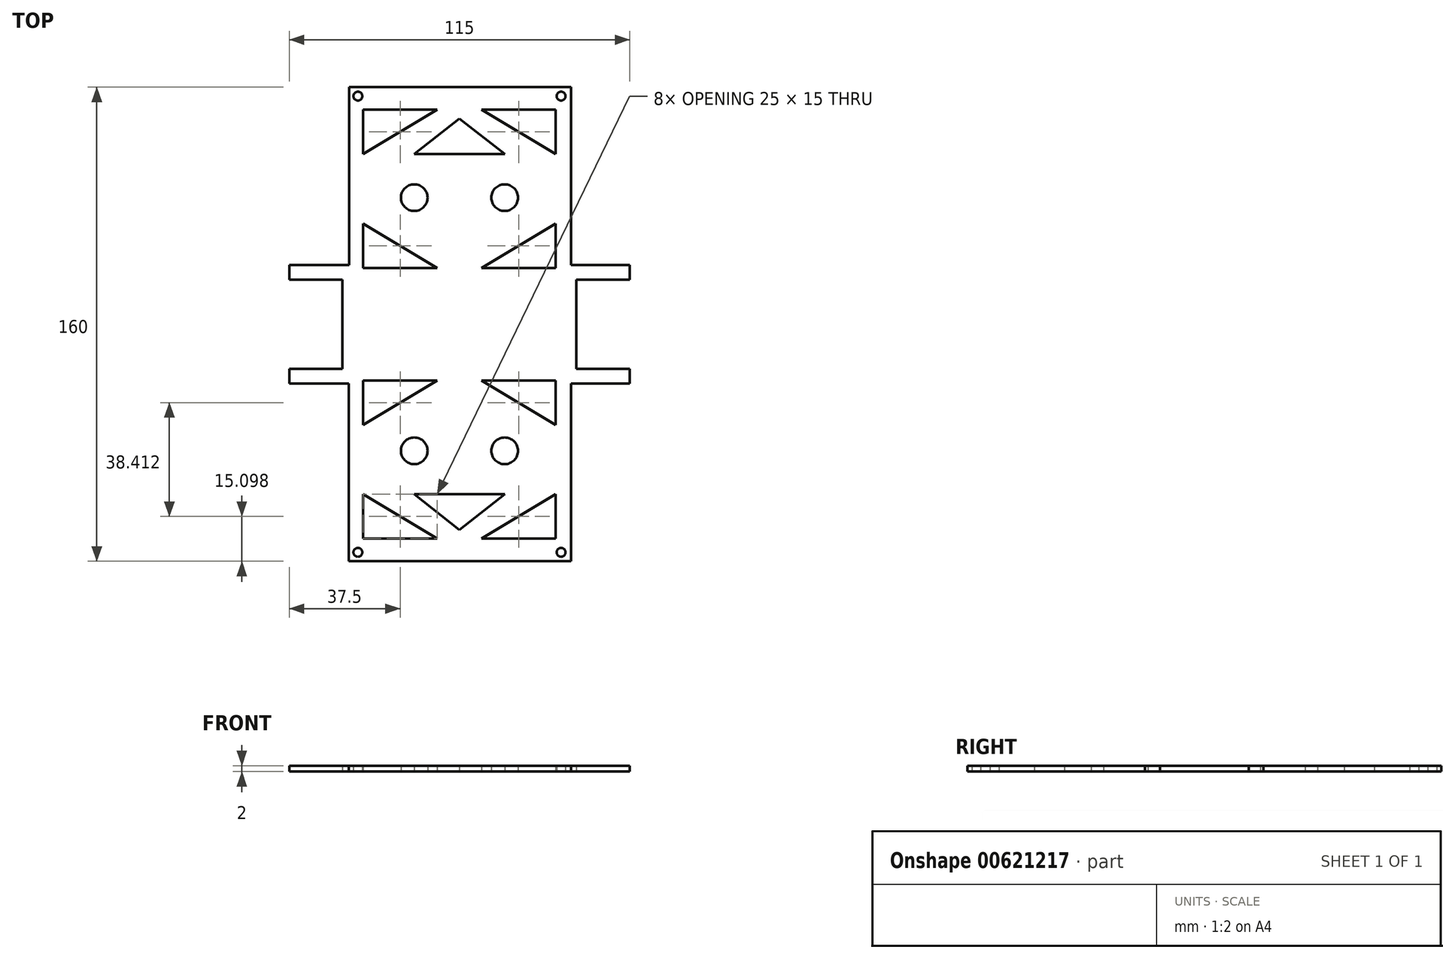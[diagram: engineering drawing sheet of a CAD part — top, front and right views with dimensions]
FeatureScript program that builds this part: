
annotation { "Feature Type Name" : "Feature", "Feature Type Description" : "" }
export const myFeature = defineFeature(function(context is Context, id is Id, definition is map)
    precondition{}
    {
        {
            var Q0;
            Q0=qCreatedBy(makeId("Top.planeOp"),FACE);
            var sketch = newSketch(context, id + "F0", { "sketchPlane" : qUnion([Q0])});
            skLineSegment(sketch, "E0.left", {"start": v(-57.5, 80) * mm, "end": v(-57.5, -80) * mm});
            skPoint(sketch, "E0.middle", {"position": v(0.2, 0.16) * mm});
            skLineSegment(sketch, "E1.bottom", {"start": v(-57.5, 80) * mm, "end": v(-37.3, 80) * mm});
            skLineSegment(sketch, "E1.top", {"start": v(-57.5, 20) * mm, "end": v(-37.3, 20) * mm});
            skLineSegment(sketch, "E1.right", {"start": v(-37.3, 80) * mm, "end": v(-37.3, 20) * mm});
            skLineSegment(sketch, "E2.MirrorCS", {"start": v(57.5, 20) * mm, "end": v(37.7, 20) * mm});
            skLineSegment(sketch, "E3.MirrorCS", {"start": v(37.7, 80) * mm, "end": v(37.7, 20) * mm});
            skLineSegment(sketch, "E4.MirrorCS", {"start": v(-57.5, -20) * mm, "end": v(-37.42, -20.02) * mm});
            skLineSegment(sketch, "E5.MirrorCS", {"start": v(-37.42, -80) * mm, "end": v(-37.42, -20.02) * mm});
            skLineSegment(sketch, "E6.MirrorCS", {"start": v(37.7, -80) * mm, "end": v(37.7, -20) * mm});
            skLineSegment(sketch, "E7.MirrorCS", {"start": v(57.5, -20) * mm, "end": v(37.7, -20) * mm});
            skLineSegment(sketch, "E8.bottom", {"start": v(57.5, -80) * mm, "end": v(-57.5, -80) * mm});
            skLineSegment(sketch, "E8.top", {"start": v(57.5, 80) * mm, "end": v(-57.5, 80) * mm});
            skLineSegment(sketch, "E8.left", {"start": v(57.5, -80) * mm, "end": v(57.5, 80) * mm});
            skLineSegment(sketch, "E8.right", {"start": v(-57.5, -80) * mm, "end": v(-57.5, 80) * mm});
            skPoint(sketch, "E8.middle", {"position": v(0, 0) * mm});
            skCircle(sketch, "E9", {"center": v(-15.27, 42.73) * mm, "radius": 4.5 * mm});
            skCircle(sketch, "E10.MirrorC", {"center": v(15.27, 42.73) * mm, "radius": 4.5 * mm});
            skCircle(sketch, "E11.MirrorC", {"center": v(-15.27, -42.73) * mm, "radius": 4.5 * mm});
            skCircle(sketch, "E12.MirrorC", {"center": v(15.27, -42.73) * mm, "radius": 4.5 * mm});
            skLineSegment(sketch, "E13", {"start": v(32.5, -72.4) * mm, "end": v(32.5, -57.4) * mm});
            skLineSegment(sketch, "E14", {"start": v(32.5, -57.4) * mm, "end": v(7.5, -72.4) * mm});
            skLineSegment(sketch, "E15", {"start": v(7.5, -72.4) * mm, "end": v(32.5, -72.4) * mm});
            skLineSegment(sketch, "E16.MirrorCS", {"start": v(32.5, 57.4) * mm, "end": v(7.5, 72.4) * mm});
            skLineSegment(sketch, "E17.MirrorCS", {"start": v(32.5, 72.4) * mm, "end": v(32.5, 57.4) * mm});
            skLineSegment(sketch, "E18.MirrorCS", {"start": v(7.5, 72.4) * mm, "end": v(32.5, 72.4) * mm});
            skLineSegment(sketch, "E19.MirrorCS", {"start": v(-32.5, -57.4) * mm, "end": v(-7.5, -72.4) * mm});
            skLineSegment(sketch, "E20.MirrorCS", {"start": v(-32.5, -72.4) * mm, "end": v(-32.5, -57.4) * mm});
            skLineSegment(sketch, "E21.MirrorCS", {"start": v(-7.5, -72.4) * mm, "end": v(-32.5, -72.4) * mm});
            skLineSegment(sketch, "E22.MirrorCS", {"start": v(-32.5, 57.4) * mm, "end": v(-7.5, 72.4) * mm});
            skLineSegment(sketch, "E23.MirrorCS", {"start": v(-32.5, 72.4) * mm, "end": v(-32.5, 57.4) * mm});
            skLineSegment(sketch, "E24.MirrorCS", {"start": v(-7.5, 72.4) * mm, "end": v(-32.5, 72.4) * mm});
            skLineSegment(sketch, "E25", {"start": v(-63.13, 45.7) * mm, "end": v(61.99, 45.7) * mm, "construction": true});
            skLineSegment(sketch, "E26.MirrorCS", {"start": v(-32.5, 34) * mm, "end": v(-7.5, 19) * mm});
            skLineSegment(sketch, "E27.MirrorCS", {"start": v(-7.5, 19) * mm, "end": v(-32.5, 19) * mm});
            skLineSegment(sketch, "E28.MirrorCS", {"start": v(-32.5, 19) * mm, "end": v(-32.5, 34) * mm});
            skLineSegment(sketch, "E29.MirrorCS", {"start": v(7.5, 19) * mm, "end": v(32.5, 19) * mm});
            skLineSegment(sketch, "E30.MirrorCS", {"start": v(32.5, 19) * mm, "end": v(32.5, 34) * mm});
            skLineSegment(sketch, "E31.MirrorCS", {"start": v(32.5, 34) * mm, "end": v(7.5, 19) * mm});
            skLineSegment(sketch, "E32.MirrorCS", {"start": v(-7.5, -19) * mm, "end": v(-32.5, -19) * mm});
            skLineSegment(sketch, "E33.MirrorCS", {"start": v(-32.5, -34) * mm, "end": v(-7.5, -19) * mm});
            skLineSegment(sketch, "E34.MirrorCS", {"start": v(-32.5, -19) * mm, "end": v(-32.5, -34) * mm});
            skLineSegment(sketch, "E35.MirrorCS", {"start": v(7.5, -19) * mm, "end": v(32.5, -19) * mm});
            skLineSegment(sketch, "E36.MirrorCS", {"start": v(32.5, -34) * mm, "end": v(7.5, -19) * mm});
            skLineSegment(sketch, "E37.MirrorCS", {"start": v(32.5, -19) * mm, "end": v(32.5, -34) * mm});
            skLineSegment(sketch, "E38", {"start": v(-15.27, -57.4) * mm, "end": v(15.27, -57.4) * mm});
            skLineSegment(sketch, "E39", {"start": v(15.27, -57.4) * mm, "end": v(0, -69.36) * mm});
            skLineSegment(sketch, "E40", {"start": v(0, -69.36) * mm, "end": v(-15.27, -57.4) * mm});
            skLineSegment(sketch, "E41.MirrorCS", {"start": v(-15.27, 57.4) * mm, "end": v(15.27, 57.4) * mm});
            skLineSegment(sketch, "E42.MirrorCS", {"start": v(0, 69.36) * mm, "end": v(-15.27, 57.4) * mm});
            skLineSegment(sketch, "E43.MirrorCS", {"start": v(15.27, 57.4) * mm, "end": v(0, 69.36) * mm});
            skLineSegment(sketch, "E44.bottom", {"start": v(-57.5, 15) * mm, "end": v(-39.5, 15) * mm});
            skLineSegment(sketch, "E44.top", {"start": v(-57.5, -15) * mm, "end": v(-39.5, -15) * mm});
            skLineSegment(sketch, "E44.left", {"start": v(-57.5, 15) * mm, "end": v(-57.5, -15) * mm});
            skLineSegment(sketch, "E44.right", {"start": v(-39.5, 15) * mm, "end": v(-39.5, -15) * mm});
            skLineSegment(sketch, "E45.MirrorCS", {"start": v(39.5, 15) * mm, "end": v(39.5, -15) * mm});
            skLineSegment(sketch, "E46.MirrorCS", {"start": v(57.5, 15) * mm, "end": v(39.5, 15) * mm});
            skLineSegment(sketch, "E47.MirrorCS", {"start": v(57.5, -15) * mm, "end": v(39.5, -15) * mm});
            skCircle(sketch, "E48", {"center": v(-34.3, 77) * mm, "radius": 1.5 * mm});
            skCircle(sketch, "E49.MirrorC", {"center": v(34.3, 77) * mm, "radius": 1.5 * mm});
            skCircle(sketch, "E50.MirrorC", {"center": v(-34.3, -77) * mm, "radius": 1.5 * mm});
            skCircle(sketch, "E51.MirrorC", {"center": v(34.3, -77) * mm, "radius": 1.5 * mm});
            skSolve(sketch);
        }
        {
            var Q0;
            {var subQ1=sQuery(id+"F0.wireOp",EDGE,"E1.top");Q0=makeQuery(id+"F0.imprint","IMPRINT",FACE,{"disambiguationData":[TD([[makeQuery(id+"F0.imprint","IMPRINT",EDGE,{"derivedFrom":subQ1}),-1.0]])]});}
            extrude(context, id + "F1", {"entities" : qUnion([Q0]), "depth" : 2 * mm, "offsetDistance" : 25 * mm});
        }
    });
